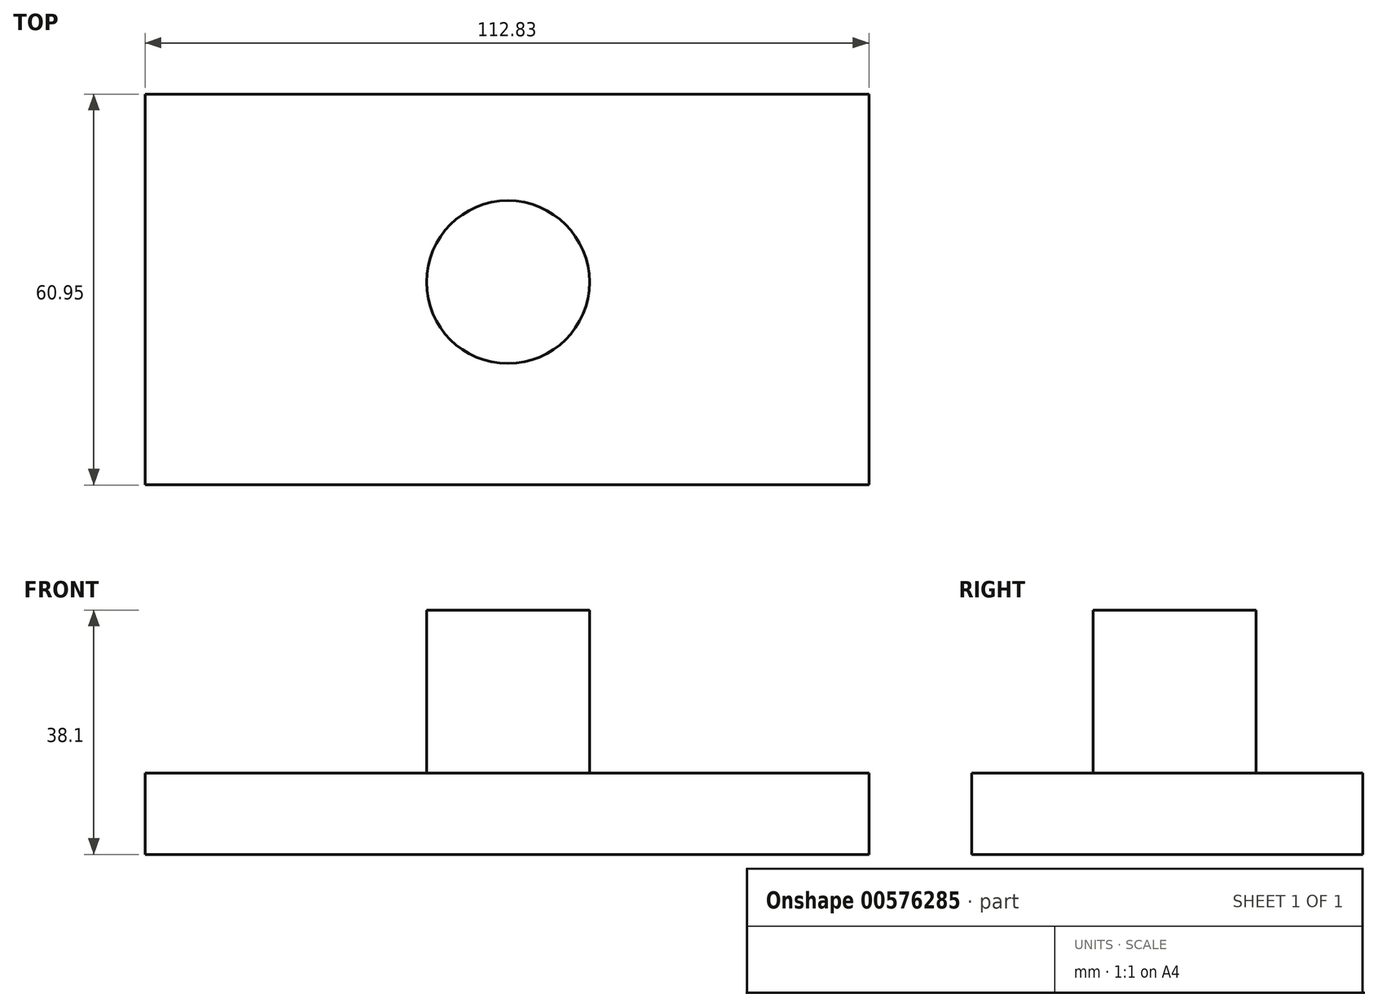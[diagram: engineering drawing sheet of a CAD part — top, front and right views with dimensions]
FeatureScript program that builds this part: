
annotation { "Feature Type Name" : "Feature", "Feature Type Description" : "" }
export const myFeature = defineFeature(function(context is Context, id is Id, definition is map)
    precondition{}
    {
        {
            var Q0;
            Q0=qCreatedBy(makeId("Top.planeOp"),FACE);
            var sketch = newSketch(context, id + "F0", { "sketchPlane" : qUnion([Q0])});
            skLineSegment(sketch, "E0.top", {"start": v(0, -31.63) * mm, "end": v(56.27, -31.63) * mm});
            skLineSegment(sketch, "E0.right", {"start": v(56.27, 0) * mm, "end": v(56.27, -31.63) * mm});
            skLineSegment(sketch, "E1.top", {"start": v(0, 29.32) * mm, "end": v(-56.56, 29.32) * mm});
            skLineSegment(sketch, "E1.right", {"start": v(-56.56, 0) * mm, "end": v(-56.56, 29.32) * mm});
            skLineSegment(sketch, "E2.top", {"start": v(-56.56, -31.63) * mm, "end": v(0, -31.63) * mm});
            skLineSegment(sketch, "E2.left", {"start": v(-56.56, 0) * mm, "end": v(-56.56, -31.63) * mm});
            skLineSegment(sketch, "E3.bottom", {"start": v(0, 29.32) * mm, "end": v(56.27, 29.32) * mm});
            skLineSegment(sketch, "E3.right", {"start": v(56.27, 29.32) * mm, "end": v(56.27, 0) * mm});
            skSolve(sketch);
        }
        {
            var Q0;
            Q0 = qSketchRegion(id + "F0", true);
            extrude(context, id + "F1", {"entities" : qUnion([Q0]), "depth" : 12.7 * mm, "offsetDistance" : 25.4 * mm});
        }
        {
            var Q0;
            Q0=qCreatedBy(makeId("Front.planeOp"),FACE);
            var sketch = newSketch(context, id + "F2", { "sketchPlane" : qUnion([Q0])});
            skLineSegment(sketch, "E4.bottom", {"start": v(0, 12.7) * mm, "end": v(12.7, 12.7) * mm});
            skLineSegment(sketch, "E4.top", {"start": v(0, 38.1) * mm, "end": v(12.7, 38.1) * mm});
            skLineSegment(sketch, "E4.left", {"start": v(0, 12.7) * mm, "end": v(0, 38.1) * mm});
            skLineSegment(sketch, "E4.right", {"start": v(12.7, 12.7) * mm, "end": v(12.7, 38.1) * mm});
            skSolve(sketch);
        }
        {
            var Q0;
            Q0=makeQuery(id+"F2.imprint","IMPRINT",FACE,{"disambiguationData":[TD([[makeQuery(id+"F2.imprint","IMPRINT",EDGE,{"derivedFrom":sQuery(id+"F2.wireOp",EDGE,"E4.bottom")}),1.0]])]});
            var Q1;
            Q1=sQuery(id+"F2.wireOp",EDGE,"E4.left");
            revolve(context, id + "F3", {"operationType" : NewBodyOperationType.ADD, "entities" : qUnion([Q0]), "axis" : qUnion([Q1]), "revolveType" : RevolveType.FULL});
        }
    });
